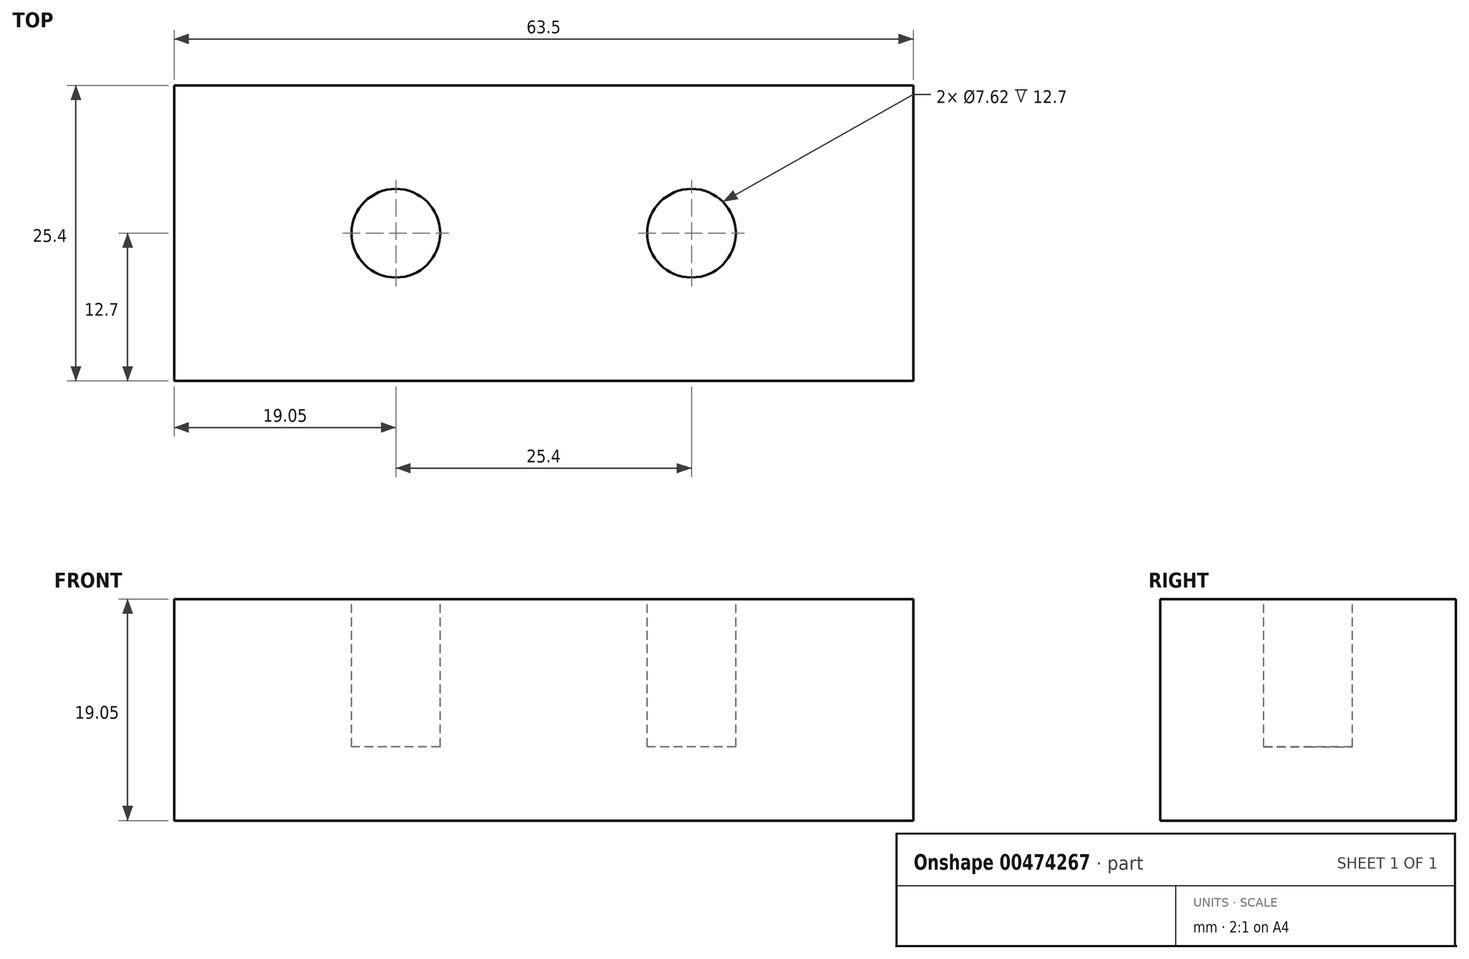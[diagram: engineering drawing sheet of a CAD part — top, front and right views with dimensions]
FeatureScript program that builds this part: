
annotation { "Feature Type Name" : "Feature", "Feature Type Description" : "" }
export const myFeature = defineFeature(function(context is Context, id is Id, definition is map)
    precondition{}
    {
        {
            var Q0;
            Q0=qCreatedBy(makeId("Front.planeOp"),FACE);
            var sketch = newSketch(context, id + "F0", { "sketchPlane" : qUnion([Q0])});
            skLineSegment(sketch, "E0", {"start": v(0, 0) * mm, "end": v(63.5, 0) * mm});
            skLineSegment(sketch, "E1", {"start": v(63.5, 0) * mm, "end": v(63.5, -19.05) * mm});
            skLineSegment(sketch, "E2", {"start": v(63.5, -19.05) * mm, "end": v(0, -19.05) * mm});
            skLineSegment(sketch, "E3", {"start": v(0, -19.05) * mm, "end": v(0, 0) * mm});
            skSolve(sketch);
        }
        {
            var Q0;
            Q0 = qSketchRegion(id + "F0", true);
            extrude(context, id + "F1", {"entities" : qUnion([Q0]), "endBound" : BoundingType.SYMMETRIC, "depth" : 25.4 * mm});
        }
        {
            var Q0;
            Q0=makeQuery(id+"F1.opExtrude","SWEPT_FACE",FACE,{"disambiguationData":[OSD([sQuery(id+"F0.wireOp",EDGE,"E0")])]});
            var sketch = newSketch(context, id + "F2", { "sketchPlane" : qUnion([Q0])});
            skCircle(sketch, "E4", {"center": v(44.45, 0) * mm, "radius": 3.81 * mm});
            skLineSegment(sketch, "E5", {"start": v(31.75, -12.7) * mm, "end": v(31.75, 12.7) * mm, "construction": true});
            skCircle(sketch, "E6.MirrorC", {"center": v(19.05, 0) * mm, "radius": 3.81 * mm});
            skSolve(sketch);
        }
        {
            var Q0;
            Q0 = qSketchRegion(id + "F2", true);
            var Q1;
            Q1 = qSketchRegion(id + "F4", true);
            extrude(context, id + "F3", {"entities" : qUnion([Q0, Q1]), "operationType" : NewBodyOperationType.REMOVE, "oppositeDirection" : true, "depth" : 12.7 * mm});
        }
    });
